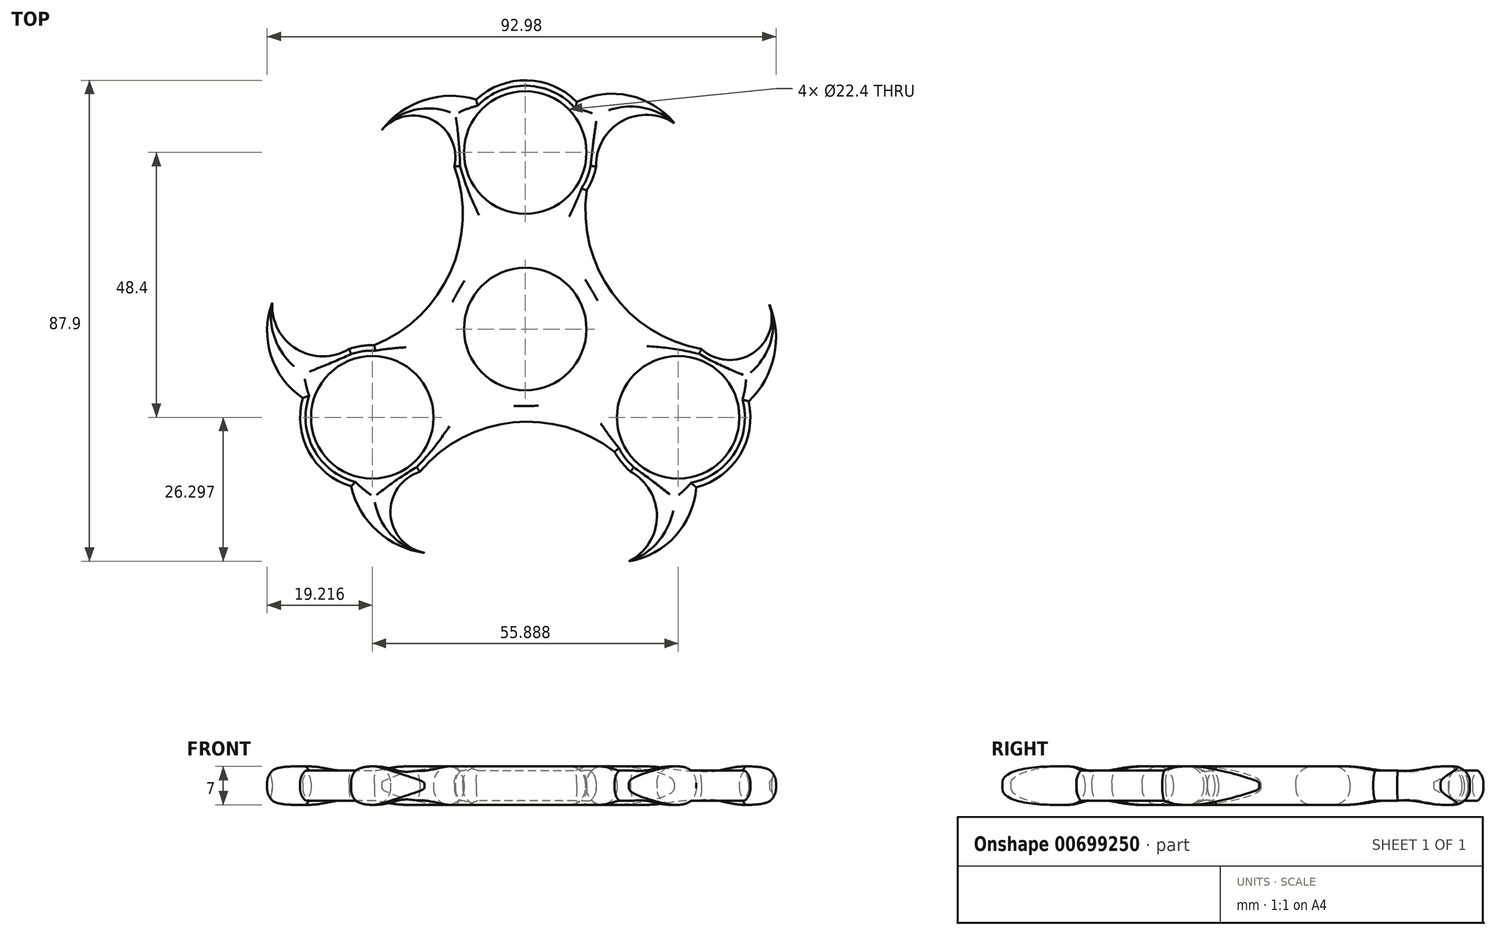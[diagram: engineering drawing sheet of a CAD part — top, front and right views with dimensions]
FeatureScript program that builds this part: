
annotation { "Feature Type Name" : "Feature", "Feature Type Description" : "" }
export const myFeature = defineFeature(function(context is Context, id is Id, definition is map)
    precondition{}
    {
        {
            var Q0;
            Q0=qCreatedBy(makeId("Top.planeOp"),FACE);
            var sketch = newSketch(context, id + "F0", { "sketchPlane" : qUnion([Q0])});
            skCircle(sketch, "E0", {"center": v(0, 0) * mm, "radius": 11.2 * mm});
            skCircle(sketch, "E1", {"center": v(0, 32.27) * mm, "radius": 11.2 * mm});
            skArc(sketch, "E2", {"start": v(11.24, 25.35) * mm, "mid": v(1.03, 45.43) * mm, "end": v(-12.18, 27.18) * mm});
            skCircle(sketch, "E3.1.0", {"center": v(-27.94, -16.13) * mm, "radius": 11.2 * mm});
            skArc(sketch, "E3.1.1", {"start": v(-27.58, -2.94) * mm, "mid": v(-39.86, -21.82) * mm, "end": v(-17.45, -24.14) * mm});
            skCircle(sketch, "E3.2.0", {"center": v(27.94, -16.13) * mm, "radius": 11.2 * mm});
            skArc(sketch, "E3.2.1", {"start": v(16.33, -22.41) * mm, "mid": v(38.83, -23.6) * mm, "end": v(29.63, -3.04) * mm});
            skArc(sketch, "E4", {"start": v(-27.58, -2.94) * mm, "mid": v(-13.67, 10.44) * mm, "end": v(-12.95, 29.72) * mm});
            skArc(sketch, "E5.1.0", {"start": v(16.33, -22.41) * mm, "mid": v(-2.2, -17.06) * mm, "end": v(-19.26, -26.08) * mm});
            skArc(sketch, "E5.2.0", {"start": v(11.24, 25.35) * mm, "mid": v(15.88, 6.62) * mm, "end": v(32.22, -3.64) * mm});
            skArc(sketch, "E6", {"start": v(-8.97, 41.95) * mm, "mid": v(-19.22, 41.58) * mm, "end": v(-27.12, 35.05) * mm});
            skArc(sketch, "E7", {"start": v(-12.95, 29.72) * mm, "mid": v(-17.72, 38.55) * mm, "end": v(-27.12, 35.05) * mm});
            skArc(sketch, "E8", {"start": v(27.27, 37.63) * mm, "mid": v(19.02, 42.67) * mm, "end": v(9.42, 41.52) * mm});
            skArc(sketch, "E9", {"start": v(27.27, 37.63) * mm, "mid": v(17.72, 38.01) * mm, "end": v(12.95, 29.72) * mm});
            skArc(sketch, "E10.1.0", {"start": v(-46.22, 4.8) * mm, "mid": v(-41.78, -3.66) * mm, "end": v(-32.22, -3.64) * mm});
            skArc(sketch, "E10.1.1", {"start": v(-46.22, 4.8) * mm, "mid": v(-46.46, -4.86) * mm, "end": v(-40.66, -12.6) * mm});
            skArc(sketch, "E10.1.2", {"start": v(-31.84, -28.74) * mm, "mid": v(-26.4, -37.43) * mm, "end": v(-16.8, -41.02) * mm});
            skArc(sketch, "E10.1.3", {"start": v(-19.26, -26.08) * mm, "mid": v(-24.53, -34.62) * mm, "end": v(-16.8, -41.02) * mm});
            skArc(sketch, "E10.2.0", {"start": v(18.95, -42.43) * mm, "mid": v(24.06, -34.35) * mm, "end": v(19.26, -26.08) * mm});
            skArc(sketch, "E10.2.1", {"start": v(18.95, -42.43) * mm, "mid": v(27.44, -37.8) * mm, "end": v(31.24, -28.91) * mm});
            skArc(sketch, "E10.2.2", {"start": v(40.81, -13.2) * mm, "mid": v(45.62, -4.15) * mm, "end": v(43.92, 5.97) * mm});
            skArc(sketch, "E10.2.3", {"start": v(32.22, -3.64) * mm, "mid": v(42.25, -3.93) * mm, "end": v(43.92, 5.97) * mm});
            skSolve(sketch);
        }
        {
            var Q0;
            Q0=makeQuery(id+"F0.imprint","IMPRINT",FACE,{"disambiguationData":[TD([[makeQuery(id+"F0.imprint","IMPRINT",EDGE,{"derivedFrom":sQuery(id+"F0.wireOp",EDGE,"E0")}),-1.0]])]});
            var Q1;
            {var subQ0=sQuery(id+"F0.wireOp",EDGE,"E6");var subQ1=sQuery(id+"F0.wireOp",EDGE,"E2");var subQ2=makeQuery(id+"F0.imprint","INTERSECT",VERTEX,{"derivedFrom":[subQ1,subQ0]});Q1=makeQuery(id+"F0.imprint","IMPRINT",FACE,{"disambiguationData":[TD([[makeQuery(id+"F0.imprint","IMPRINT",EDGE,{"disambiguationData":[TD([[subQ2,-1.0]])],"derivedFrom":subQ1}),-1.0]])]});}
            var Q2;
            {var subQ0=sQuery(id+"F0.wireOp",EDGE,"E8");Q2=makeQuery(id+"F0.imprint","IMPRINT",FACE,{"disambiguationData":[TD([[makeQuery(id+"F0.imprint","IMPRINT",EDGE,{"derivedFrom":subQ0}),1.0]])]});}
            var Q3;
            {var subQ0=sQuery(id+"F0.wireOp",EDGE,"E10.2.1");Q3=makeQuery(id+"F0.imprint","IMPRINT",FACE,{"disambiguationData":[TD([[makeQuery(id+"F0.imprint","IMPRINT",EDGE,{"derivedFrom":subQ0}),1.0]])]});}
            var Q4;
            {var subQ0=sQuery(id+"F0.wireOp",EDGE,"E10.2.2");var subQ1=sQuery(id+"F0.wireOp",EDGE,"E3.2.1");var subQ2=makeQuery(id+"F0.imprint","INTERSECT",VERTEX,{"derivedFrom":[subQ1,subQ0]});Q4=makeQuery(id+"F0.imprint","IMPRINT",FACE,{"disambiguationData":[TD([[makeQuery(id+"F0.imprint","IMPRINT",EDGE,{"disambiguationData":[TD([[subQ2,-1.0]])],"derivedFrom":subQ1}),-1.0]])]});}
            var Q5;
            {var subQ0=sQuery(id+"F0.wireOp",EDGE,"E10.1.1");Q5=makeQuery(id+"F0.imprint","IMPRINT",FACE,{"disambiguationData":[TD([[makeQuery(id+"F0.imprint","IMPRINT",EDGE,{"derivedFrom":subQ0}),1.0]])]});}
            var Q6;
            {var subQ0=sQuery(id+"F0.wireOp",EDGE,"E10.1.2");var subQ1=sQuery(id+"F0.wireOp",EDGE,"E3.1.1");var subQ2=makeQuery(id+"F0.imprint","INTERSECT",VERTEX,{"derivedFrom":[subQ1,subQ0]});Q6=makeQuery(id+"F0.imprint","IMPRINT",FACE,{"disambiguationData":[TD([[makeQuery(id+"F0.imprint","IMPRINT",EDGE,{"disambiguationData":[TD([[subQ2,-1.0]])],"derivedFrom":subQ1}),-1.0]])]});}
            extrude(context, id + "F1", {"entities" : qUnion([Q0, Q1, Q2, Q3, Q4, Q5, Q6]), "depth" : 7 * mm, "offsetDistance" : 25 * mm});
        }
        {
            var Q0;
            Q0=makeQuery(id+"F1.opExtrude","CAP_FACE",FACE,{"disambiguationData":[OSD([sQuery(id+"F0.wireOp",EDGE,"E0"),sQuery(id+"F0.wireOp",EDGE,"E1"),sQuery(id+"F0.wireOp",EDGE,"E2"),sQuery(id+"F0.wireOp",EDGE,"E3.1.0"),sQuery(id+"F0.wireOp",EDGE,"E3.1.1"),sQuery(id+"F0.wireOp",EDGE,"E3.2.0"),sQuery(id+"F0.wireOp",EDGE,"E3.2.1"),sQuery(id+"F0.wireOp",EDGE,"E4"),sQuery(id+"F0.wireOp",EDGE,"E5.1.0"),sQuery(id+"F0.wireOp",EDGE,"E5.2.0"),sQuery(id+"F0.wireOp",EDGE,"E6"),sQuery(id+"F0.wireOp",EDGE,"E7"),sQuery(id+"F0.wireOp",EDGE,"E8"),sQuery(id+"F0.wireOp",EDGE,"E9"),sQuery(id+"F0.wireOp",EDGE,"E10.1.0"),sQuery(id+"F0.wireOp",EDGE,"E10.1.1"),sQuery(id+"F0.wireOp",EDGE,"E10.1.2"),sQuery(id+"F0.wireOp",EDGE,"E10.1.3"),sQuery(id+"F0.wireOp",EDGE,"E10.2.0"),sQuery(id+"F0.wireOp",EDGE,"E10.2.1"),sQuery(id+"F0.wireOp",EDGE,"E10.2.2"),sQuery(id+"F0.wireOp",EDGE,"E10.2.3")])],"isStart":false});
            fillet(context, id + "F2", {"entities" : qUnion([Q0]), "radius" : 3 * mm, "tangentPropagation" : true, "allowEdgeOverflow" : false});
        }
        {
            var Q0;
            Q0=makeQuery(id+"F1.opExtrude","CAP_FACE",FACE,{"disambiguationData":[OSD([sQuery(id+"F0.wireOp",EDGE,"E0"),sQuery(id+"F0.wireOp",EDGE,"E1"),sQuery(id+"F0.wireOp",EDGE,"E2"),sQuery(id+"F0.wireOp",EDGE,"E3.1.0"),sQuery(id+"F0.wireOp",EDGE,"E3.1.1"),sQuery(id+"F0.wireOp",EDGE,"E3.2.0"),sQuery(id+"F0.wireOp",EDGE,"E3.2.1"),sQuery(id+"F0.wireOp",EDGE,"E4"),sQuery(id+"F0.wireOp",EDGE,"E5.1.0"),sQuery(id+"F0.wireOp",EDGE,"E5.2.0"),sQuery(id+"F0.wireOp",EDGE,"E6"),sQuery(id+"F0.wireOp",EDGE,"E7"),sQuery(id+"F0.wireOp",EDGE,"E8"),sQuery(id+"F0.wireOp",EDGE,"E9"),sQuery(id+"F0.wireOp",EDGE,"E10.1.0"),sQuery(id+"F0.wireOp",EDGE,"E10.1.1"),sQuery(id+"F0.wireOp",EDGE,"E10.1.2"),sQuery(id+"F0.wireOp",EDGE,"E10.1.3"),sQuery(id+"F0.wireOp",EDGE,"E10.2.0"),sQuery(id+"F0.wireOp",EDGE,"E10.2.1"),sQuery(id+"F0.wireOp",EDGE,"E10.2.2"),sQuery(id+"F0.wireOp",EDGE,"E10.2.3")])],"isStart":true});
            var Q1;
            Q1=makeQuery(id+"F1.opExtrude","CAP_EDGE",EDGE,{"disambiguationData":[OSD([sQuery(id+"F0.wireOp",EDGE,"E3.2.0")])],"isStart":true});
            var Q2;
            Q2=makeQuery(id+"F1.opExtrude","CAP_EDGE",EDGE,{"disambiguationData":[OSD([sQuery(id+"F0.wireOp",EDGE,"E3.1.0")])],"isStart":true});
            var Q3;
            {var subQ0=sQuery(id+"F0.wireOp",EDGE,"E3.1.0");Q3=makeQuery(id+"F2.opFillet","BLEND_EDGE",EDGE,{"blendedFrom":[makeQuery(id+"F1.opExtrude","CAP_EDGE",EDGE,{"disambiguationData":[OSD([subQ0])],"isStart":false}),makeQuery(id+"F1.opExtrude","SWEPT_FACE",FACE,{"disambiguationData":[OSD([subQ0])]})],"blendedInto":[makeQuery(id+"F1.opExtrude","SWEPT_FACE",FACE,{"disambiguationData":[OSD([subQ0])]})]});}
            var Q4;
            {var subQ0=sQuery(id+"F0.wireOp",EDGE,"E1");Q4=makeQuery(id+"F2.opFillet","BLEND_EDGE",EDGE,{"blendedFrom":[makeQuery(id+"F1.opExtrude","CAP_EDGE",EDGE,{"disambiguationData":[OSD([subQ0])],"isStart":false}),makeQuery(id+"F1.opExtrude","SWEPT_FACE",FACE,{"disambiguationData":[OSD([subQ0])]})],"blendedInto":[makeQuery(id+"F1.opExtrude","SWEPT_FACE",FACE,{"disambiguationData":[OSD([subQ0])]})]});}
            var Q5;
            {var subQ0=sQuery(id+"F0.wireOp",EDGE,"E0");Q5=makeQuery(id+"F2.opFillet","BLEND_EDGE",EDGE,{"blendedFrom":[makeQuery(id+"F1.opExtrude","CAP_EDGE",EDGE,{"disambiguationData":[OSD([subQ0])],"isStart":false}),makeQuery(id+"F1.opExtrude","SWEPT_FACE",FACE,{"disambiguationData":[OSD([subQ0])]})],"blendedInto":[makeQuery(id+"F1.opExtrude","SWEPT_FACE",FACE,{"disambiguationData":[OSD([subQ0])]})]});}
            fillet(context, id + "F3", {"entities" : qUnion([Q0, Q1, Q2, Q3, Q4, Q5]), "radius" : 3 * mm, "tangentPropagation" : true, "allowEdgeOverflow" : false});
        }
    });
